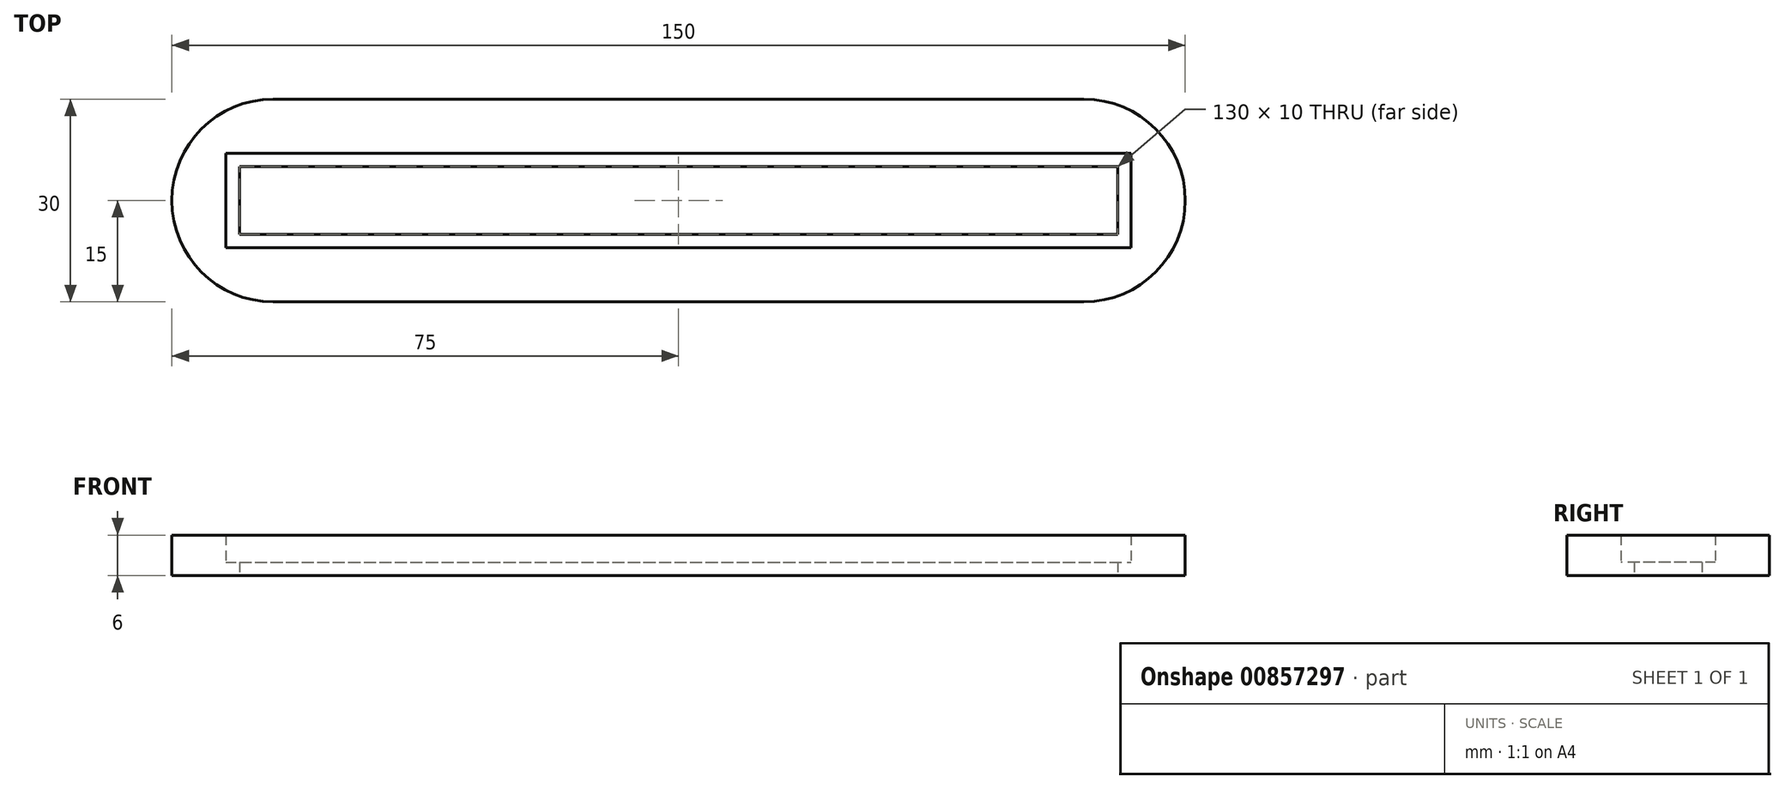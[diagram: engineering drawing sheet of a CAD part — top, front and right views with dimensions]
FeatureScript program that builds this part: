
annotation { "Feature Type Name" : "Feature", "Feature Type Description" : "" }
export const myFeature = defineFeature(function(context is Context, id is Id, definition is map)
    precondition{}
    {
        {
            var Q0;
            Q0=qCreatedBy(makeId("Top.planeOp"),FACE);
            var sketch = newSketch(context, id + "F0", { "sketchPlane" : qUnion([Q0])});
            skLineSegment(sketch, "E0.bottom", {"start": v(-75, 15) * mm, "end": v(75, 15) * mm});
            skLineSegment(sketch, "E0.top", {"start": v(-75, -15) * mm, "end": v(75, -15) * mm});
            skLineSegment(sketch, "E0.right", {"start": v(75, 15) * mm, "end": v(75, -15) * mm});
            skLineSegment(sketch, "E1", {"start": v(0, 15) * mm, "end": v(0, -15) * mm, "construction": true});
            skLineSegment(sketch, "E2", {"start": v(-75, 0) * mm, "end": v(75, 0) * mm, "construction": true});
            skLineSegment(sketch, "E3", {"start": v(-75, 15) * mm, "end": v(-75, -15) * mm});
            skLineSegment(sketch, "E4.bottom", {"start": v(-75, 15) * mm, "end": v(-65, 15) * mm, "construction": true});
            skLineSegment(sketch, "E4.top", {"start": v(-75, -15) * mm, "end": v(-65, -15) * mm, "construction": true});
            skLineSegment(sketch, "E4.left", {"start": v(-75, 15) * mm, "end": v(-75, -15) * mm, "construction": true});
            skLineSegment(sketch, "E4.right", {"start": v(-65, 5) * mm, "end": v(-65, -5) * mm, "construction": true});
            skLineSegment(sketch, "E5.MirrorCS", {"start": v(65, 5) * mm, "end": v(65, -5) * mm, "construction": true});
            skLineSegment(sketch, "E6", {"start": v(-65, 3.72) * mm, "end": v(-65, 5) * mm, "construction": true});
            skLineSegment(sketch, "E7", {"start": v(-65, 0) * mm, "end": v(-62.88, 0) * mm, "construction": true});
            skLineSegment(sketch, "E8.bottom", {"start": v(-65, 5) * mm, "end": v(65, 5) * mm});
            skLineSegment(sketch, "E8.top", {"start": v(-65, -5) * mm, "end": v(65, -5) * mm});
            skLineSegment(sketch, "E8.left", {"start": v(-65, 5) * mm, "end": v(-65, -5) * mm});
            skLineSegment(sketch, "E8.right", {"start": v(65, 5) * mm, "end": v(65, -5) * mm});
            skPoint(sketch, "E9.orphan", {"position": v(65, -15) * mm});
            skPoint(sketch, "E10.orphan", {"position": v(65, 15) * mm});
            skLineSegment(sketch, "E11.0", {"start": v(-67, 7) * mm, "end": v(67, 7) * mm});
            skLineSegment(sketch, "E11.1", {"start": v(-67, 7) * mm, "end": v(-67, -7) * mm});
            skLineSegment(sketch, "E11.2", {"start": v(-67, -7) * mm, "end": v(67, -7) * mm});
            skLineSegment(sketch, "E11.3", {"start": v(67, 7) * mm, "end": v(67, -7) * mm});
            skLineSegment(sketch, "E12", {"start": v(-75, 0) * mm, "end": v(-45, 0) * mm, "construction": true});
            skCircle(sketch, "E13", {"center": v(-60, 0) * mm, "radius": 15 * mm});
            skCircle(sketch, "E14.MirrorC", {"center": v(60, 0) * mm, "radius": 15 * mm});
            skSolve(sketch);
        }
        {
            var Q0;
            {var subQ1=sQuery(id+"F0.wireOp",EDGE,"E11.1");Q0=makeQuery(id+"F0.imprint","IMPRINT",FACE,{"disambiguationData":[TD([[makeQuery(id+"F0.imprint","IMPRINT",EDGE,{"derivedFrom":subQ1}),-1.0]])]});}
            var Q1;
            {var subQ4=sQuery(id+"F0.wireOp",EDGE,"E11.3");Q1=makeQuery(id+"F0.imprint","IMPRINT",FACE,{"disambiguationData":[TD([[makeQuery(id+"F0.imprint","IMPRINT",EDGE,{"derivedFrom":subQ4}),1.0]])]});}
            var Q2;
            {var subQ0=sQuery(id+"F0.wireOp",EDGE,"E13");var subQ1=sQuery(id+"F0.wireOp",EDGE,"E0.top");var subQ2=makeQuery(id+"F0.imprint","INTERSECT",VERTEX,{"derivedFrom":[subQ1,subQ0]});Q2=makeQuery(id+"F0.imprint","IMPRINT",FACE,{"disambiguationData":[TD([[makeQuery(id+"F0.imprint","IMPRINT",EDGE,{"disambiguationData":[TD([[subQ2,-1.0]])],"derivedFrom":subQ1}),1.0]])]});}
            var Q3;
            {var subQ0=sQuery(id+"F0.wireOp",EDGE,"E13");var subQ1=sQuery(id+"F0.wireOp",EDGE,"E0.bottom");var subQ2=makeQuery(id+"F0.imprint","INTERSECT",VERTEX,{"derivedFrom":[subQ1,subQ0]});Q3=makeQuery(id+"F0.imprint","IMPRINT",FACE,{"disambiguationData":[TD([[makeQuery(id+"F0.imprint","IMPRINT",EDGE,{"disambiguationData":[TD([[subQ2,-1.0]])],"derivedFrom":subQ1}),-1.0]])]});}
            extrude(context, id + "F1", {"entities" : qUnion([Q0, Q1, Q2, Q3]), "depth" : 6 * mm, "offsetDistance" : 25 * mm});
        }
        {
            var Q0;
            Q0=makeQuery(id+"F0.imprint","IMPRINT",FACE,{"disambiguationData":[TD([[makeQuery(id+"F0.imprint","IMPRINT",EDGE,{"derivedFrom":sQuery(id+"F0.wireOp",EDGE,"E8.bottom")}),1.0]])]});
            var Q1;
            {var subQ0=sQuery(id+"F0.wireOp",EDGE,"E8.left");Q1=makeQuery(id+"F0.imprint","IMPRINT",FACE,{"disambiguationData":[TD([[makeQuery(id+"F0.imprint","IMPRINT",EDGE,{"derivedFrom":subQ0}),-1.0]])]});}
            var Q2;
            {var subQ4=sQuery(id+"F0.wireOp",EDGE,"E8.right");Q2=makeQuery(id+"F0.imprint","IMPRINT",FACE,{"disambiguationData":[TD([[makeQuery(id+"F0.imprint","IMPRINT",EDGE,{"derivedFrom":subQ4}),1.0]])]});}
            var Q3;
            {var subQ0=sQuery(id+"F0.wireOp",EDGE,"E13");var subQ1=sQuery(id+"F0.wireOp",EDGE,"E8.top");var subQ2=makeQuery(id+"F0.imprint","INTERSECT",VERTEX,{"derivedFrom":[subQ1,subQ0]});Q3=makeQuery(id+"F0.imprint","IMPRINT",FACE,{"disambiguationData":[TD([[makeQuery(id+"F0.imprint","IMPRINT",EDGE,{"disambiguationData":[TD([[subQ2,-1.0]])],"derivedFrom":subQ1}),-1.0]])]});}
            extrude(context, id + "F2", {"entities" : qUnion([Q0, Q1, Q2, Q3]), "operationType" : NewBodyOperationType.ADD, "depth" : 2 * mm, "offsetDistance" : 25 * mm});
        }
    });
